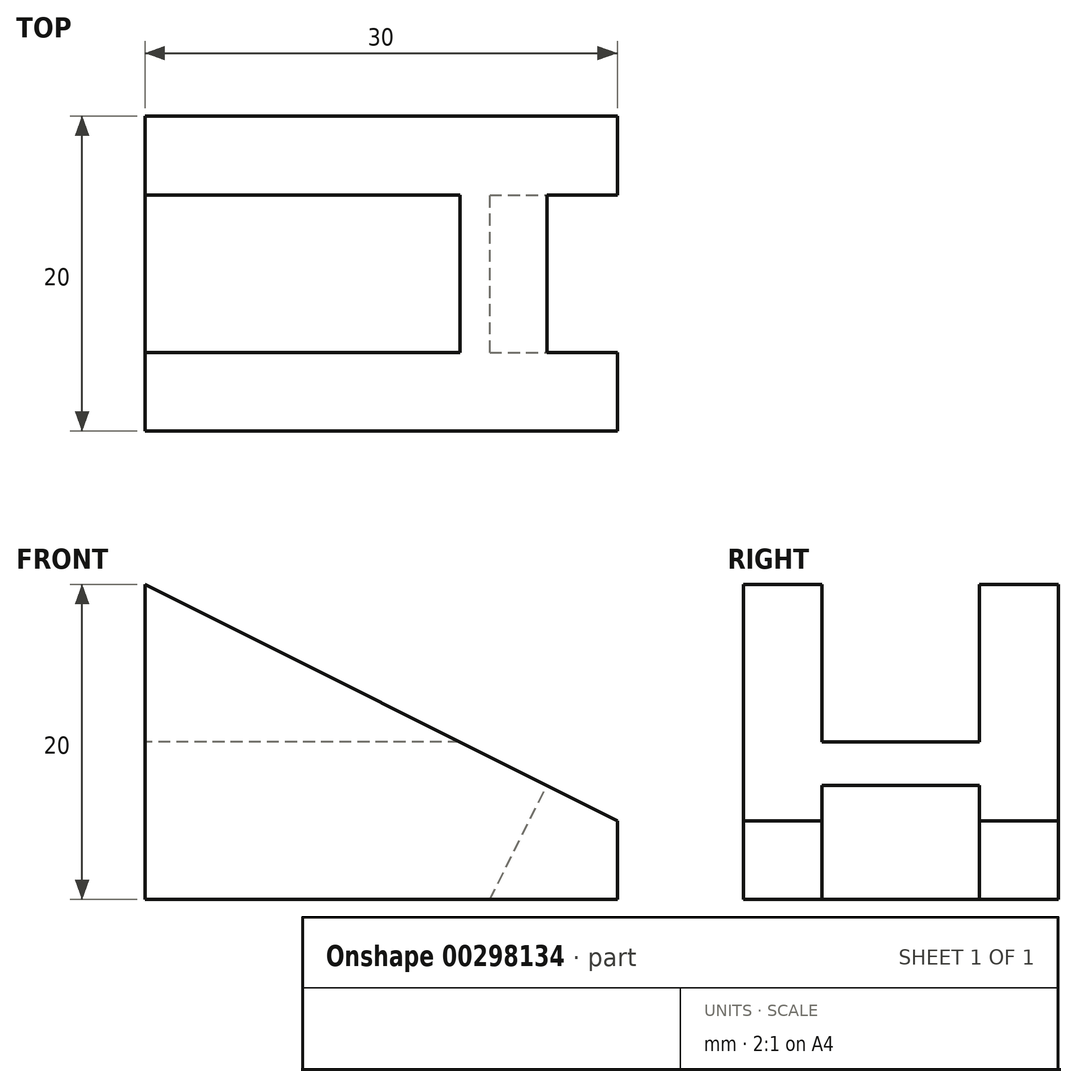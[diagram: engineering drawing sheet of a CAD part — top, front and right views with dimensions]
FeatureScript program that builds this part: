
annotation { "Feature Type Name" : "Feature", "Feature Type Description" : "" }
export const myFeature = defineFeature(function(context is Context, id is Id, definition is map)
    precondition{}
    {
        {
            var Q0;
            Q0=qCreatedBy(makeId("Front.planeOp"),FACE);
            var sketch = newSketch(context, id + "F0", { "sketchPlane" : qUnion([Q0])});
            skLineSegment(sketch, "E0", {"start": v(0, 0) * mm, "end": v(0, 20) * mm});
            skLineSegment(sketch, "E1", {"start": v(30, 0) * mm, "end": v(0, 0) * mm});
            skLineSegment(sketch, "E2", {"start": v(30, 0) * mm, "end": v(30, 5) * mm});
            skLineSegment(sketch, "E3", {"start": v(30, 5) * mm, "end": v(0, 20) * mm});
            skSolve(sketch);
        }
        {
            var Q0;
            Q0 = qSketchRegion(id + "F0", true);
            extrude(context, id + "F1", {"entities" : qUnion([Q0]), "depth" : 20 * mm});
        }
        {
            var Q0;
            Q0=makeQuery(id+"F1.opExtrude","SWEPT_FACE",FACE,{"disambiguationData":[OSD([sQuery(id+"F0.wireOp",EDGE,"E3")])]});
            var sketch = newSketch(context, id + "F2", { "sketchPlane" : qUnion([Q0])});
            skLineSegment(sketch, "E4", {"start": v(24.6, -10) * mm, "end": v(-17.6, -10) * mm, "construction": true});
            skLineSegment(sketch, "E5", {"start": v(24.6, -10) * mm, "end": v(24.6, -5) * mm});
            skLineSegment(sketch, "E6", {"start": v(24.6, -5) * mm, "end": v(19.6, -5) * mm});
            skLineSegment(sketch, "E7", {"start": v(19.6, -5) * mm, "end": v(19.6, -10) * mm});
            skLineSegment(sketch, "E8.MirrorCS", {"start": v(19.6, -15) * mm, "end": v(19.6, -10) * mm});
            skLineSegment(sketch, "E9.MirrorCS", {"start": v(24.6, -15) * mm, "end": v(19.6, -15) * mm});
            skLineSegment(sketch, "E10.MirrorCS", {"start": v(24.6, -10) * mm, "end": v(24.6, -15) * mm});
            skSolve(sketch);
        }
        {
            var Q0;
            Q0 = qSketchRegion(id + "F2", true);
            extrude(context, id + "F3", {"entities" : qUnion([Q0]), "operationType" : NewBodyOperationType.REMOVE, "endBound" : BoundingType.THROUGH_ALL, "oppositeDirection" : true, "depth" : 25 * mm});
        }
        {
            var Q0;
            Q0=makeQuery(id+"F1.opExtrude","SWEPT_FACE",FACE,{"disambiguationData":[OSD([sQuery(id+"F0.wireOp",EDGE,"E2")])]});
            var sketch = newSketch(context, id + "F4", { "sketchPlane" : qUnion([Q0])});
            skLineSegment(sketch, "E11", {"start": v(-15, 5) * mm, "end": v(-15, 0) * mm});
            skLineSegment(sketch, "E12", {"start": v(-15, 0) * mm, "end": v(-5, 0) * mm});
            skLineSegment(sketch, "E13", {"start": v(-5, 0) * mm, "end": v(-5, 5) * mm});
            skLineSegment(sketch, "E14", {"start": v(-5, 5) * mm, "end": v(-15, 5) * mm});
            skSolve(sketch);
        }
        {
            var Q0;
            Q0 = qSketchRegion(id + "F4", true);
            extrude(context, id + "F5", {"entities" : qUnion([Q0]), "operationType" : NewBodyOperationType.REMOVE, "endBound" : BoundingType.UP_TO_NEXT, "oppositeDirection" : true, "depth" : 25 * mm});
        }
        {
            var Q0;
            Q0=makeQuery(id+"F1.opExtrude","SWEPT_FACE",FACE,{"disambiguationData":[OSD([sQuery(id+"F0.wireOp",EDGE,"E0")])]});
            var sketch = newSketch(context, id + "F6", { "sketchPlane" : qUnion([Q0])});
            skPoint(sketch, "E15.endSnap0", {"position": v(10, 0) * mm});
            skLineSegment(sketch, "E16", {"start": v(10, 20) * mm, "end": v(5, 20) * mm});
            skLineSegment(sketch, "E17", {"start": v(5, 20) * mm, "end": v(5, 10) * mm});
            skLineSegment(sketch, "E18", {"start": v(5, 10) * mm, "end": v(10, 10) * mm});
            skLineSegment(sketch, "E19.MirrorCS", {"start": v(15, 10) * mm, "end": v(10, 10) * mm});
            skLineSegment(sketch, "E20.MirrorCS", {"start": v(15, 20) * mm, "end": v(15, 10) * mm});
            skLineSegment(sketch, "E21.MirrorCS", {"start": v(10, 20) * mm, "end": v(15, 20) * mm});
            skSolve(sketch);
        }
        {
            var Q0;
            Q0 = qSketchRegion(id + "F6", true);
            extrude(context, id + "F7", {"entities" : qUnion([Q0]), "operationType" : NewBodyOperationType.REMOVE, "endBound" : BoundingType.THROUGH_ALL, "oppositeDirection" : true, "depth" : 25 * mm});
        }
    });
